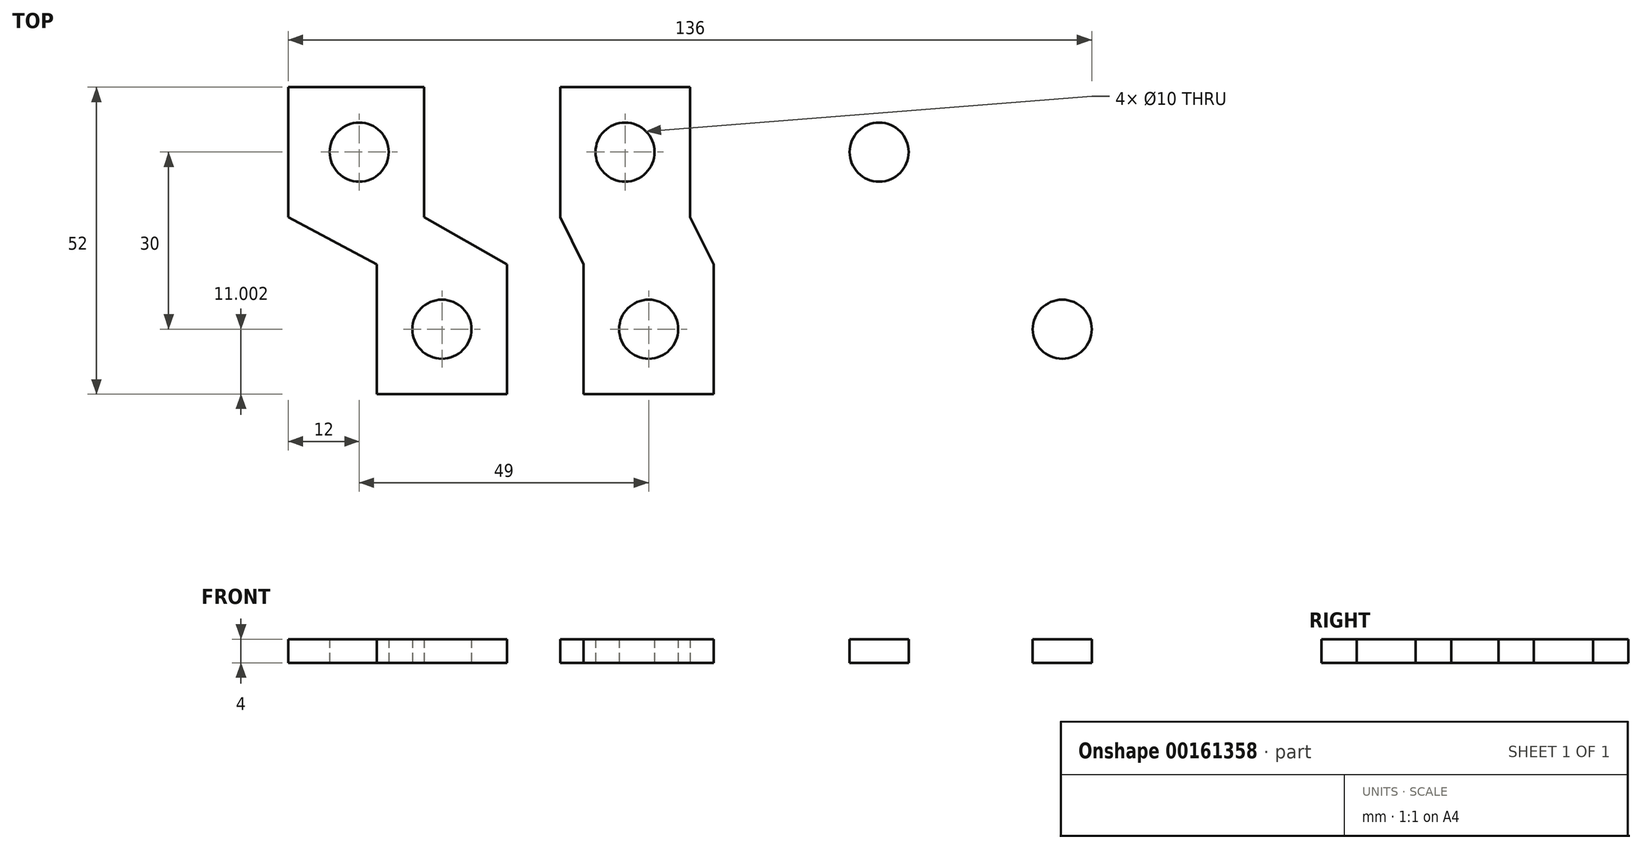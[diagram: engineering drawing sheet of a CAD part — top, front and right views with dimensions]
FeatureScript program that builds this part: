
annotation { "Feature Type Name" : "Feature", "Feature Type Description" : "" }
export const myFeature = defineFeature(function(context is Context, id is Id, definition is map)
    precondition{}
    {
        {
            var Q0;
            Q0=qCreatedBy(makeId("Top.planeOp"),FACE);
            var sketch = newSketch(context, id + "F0", { "sketchPlane" : qUnion([Q0])});
            skLineSegment(sketch, "E0.bottom", {"start": v(-56.44, 67.2) * mm, "end": v(-33.44, 67.2) * mm});
            skLineSegment(sketch, "E0.left", {"start": v(-56.44, 67.2) * mm, "end": v(-56.44, 45.2) * mm});
            skLineSegment(sketch, "E0.right", {"start": v(-33.44, 67.2) * mm, "end": v(-33.44, 45.2) * mm});
            skLineSegment(sketch, "E1.bottom", {"start": v(-41.44, 15.2) * mm, "end": v(-19.44, 15.2) * mm});
            skLineSegment(sketch, "E1.left", {"start": v(-41.44, 15.2) * mm, "end": v(-41.44, 37.2) * mm});
            skLineSegment(sketch, "E1.right", {"start": v(-19.44, 15.2) * mm, "end": v(-19.44, 37.2) * mm});
            skLineSegment(sketch, "E2", {"start": v(-56.44, 45.2) * mm, "end": v(-41.44, 37.2) * mm});
            skLineSegment(sketch, "E3", {"start": v(-33.44, 45.2) * mm, "end": v(-19.44, 37.2) * mm});
            skLineSegment(sketch, "E4.bottom", {"start": v(-10.44, 67.2) * mm, "end": v(11.56, 67.2) * mm});
            skLineSegment(sketch, "E4.left", {"start": v(-10.44, 67.2) * mm, "end": v(-10.44, 45.2) * mm});
            skLineSegment(sketch, "E4.right", {"start": v(11.56, 67.2) * mm, "end": v(11.56, 45.2) * mm});
            skLineSegment(sketch, "E5.bottom", {"start": v(-6.44, 15.2) * mm, "end": v(15.56, 15.2) * mm});
            skLineSegment(sketch, "E5.left", {"start": v(-6.44, 15.2) * mm, "end": v(-6.44, 37.2) * mm});
            skLineSegment(sketch, "E5.right", {"start": v(15.56, 15.2) * mm, "end": v(15.56, 37.2) * mm});
            skLineSegment(sketch, "E6", {"start": v(-10.44, 45.2) * mm, "end": v(-6.44, 37.2) * mm});
            skLineSegment(sketch, "E7", {"start": v(11.56, 45.2) * mm, "end": v(15.56, 37.2) * mm});
            skPoint(sketch, "E8", {"position": v(-30.44, 15.2) * mm});
            skPoint(sketch, "E9", {"position": v(-30.44, 26.2) * mm});
            skPoint(sketch, "E10", {"position": v(0.56, 56.2) * mm});
            skPoint(sketch, "E10.positionSnap0", {"position": v(0.56, 67.2) * mm});
            skPoint(sketch, "E11", {"position": v(4.56, 26.2) * mm});
            skPoint(sketch, "E11.positionSnap0", {"position": v(4.56, 15.2) * mm});
            skCircle(sketch, "E12", {"center": v(4.56, 26.2) * mm, "radius": 5 * mm});
            skCircle(sketch, "E13", {"center": v(0.56, 56.2) * mm, "radius": 5 * mm});
            skCircle(sketch, "E14", {"center": v(-30.44, 26.2) * mm, "radius": 5 * mm});
            skPoint(sketch, "E15", {"position": v(-44.44, 56.2) * mm});
            skCircle(sketch, "E16", {"center": v(-44.44, 56.2) * mm, "radius": 5 * mm});
            skLineSegment(sketch, "E17", {"start": v(15.56, 25.14) * mm, "end": v(22.06, 25.14) * mm});
            skLineSegment(sketch, "E18", {"start": v(22.06, 25.14) * mm, "end": v(22.06, 60.52) * mm});
            skPoint(sketch, "E19.MirrorP", {"position": v(43.56, 56.2) * mm});
            skCircle(sketch, "E20.MirrorC", {"center": v(43.56, 56.2) * mm, "radius": 5 * mm});
            skPoint(sketch, "E21.MirrorP", {"position": v(39.56, 26.2) * mm});
            skPoint(sketch, "E22.MirrorP", {"position": v(39.56, 15.2) * mm});
            skCircle(sketch, "E23.MirrorC", {"center": v(74.56, 26.2) * mm, "radius": 5 * mm});
            skLineSegment(sketch, "E24.MirrorCS", {"start": v(50.56, 15.2) * mm, "end": v(50.56, 37.2) * mm});
            skLineSegment(sketch, "E25.MirrorCS", {"start": v(50.56, 15.2) * mm, "end": v(28.56, 15.2) * mm});
            skLineSegment(sketch, "E26.MirrorCS", {"start": v(32.56, 67.2) * mm, "end": v(32.56, 45.2) * mm});
            skLineSegment(sketch, "E27.MirrorCS", {"start": v(54.56, 67.2) * mm, "end": v(54.56, 45.2) * mm});
            skLineSegment(sketch, "E28.MirrorCS", {"start": v(54.56, 67.2) * mm, "end": v(32.56, 67.2) * mm});
            skLineSegment(sketch, "E29.MirrorCS", {"start": v(77.56, 45.2) * mm, "end": v(63.56, 37.2) * mm});
            skLineSegment(sketch, "E30.MirrorCS", {"start": v(100.56, 45.2) * mm, "end": v(85.56, 37.2) * mm});
            skLineSegment(sketch, "E31.MirrorCS", {"start": v(63.56, 15.2) * mm, "end": v(63.56, 37.2) * mm});
            skLineSegment(sketch, "E32.MirrorCS", {"start": v(85.56, 15.2) * mm, "end": v(85.56, 37.2) * mm});
            skLineSegment(sketch, "E33.MirrorCS", {"start": v(77.56, 67.2) * mm, "end": v(77.56, 45.2) * mm});
            skPoint(sketch, "E34.MirrorP", {"position": v(74.56, 15.2) * mm});
            skLineSegment(sketch, "E35.MirrorCS", {"start": v(100.56, 67.2) * mm, "end": v(77.56, 67.2) * mm});
            skLineSegment(sketch, "E36.MirrorCS", {"start": v(32.56, 45.2) * mm, "end": v(28.56, 37.2) * mm});
            skCircle(sketch, "E37.MirrorC", {"center": v(39.56, 26.2) * mm, "radius": 5 * mm});
            skLineSegment(sketch, "E38.MirrorCS", {"start": v(85.56, 15.2) * mm, "end": v(63.56, 15.2) * mm});
            skLineSegment(sketch, "E39.MirrorCS", {"start": v(54.56, 45.2) * mm, "end": v(50.56, 37.2) * mm});
            skPoint(sketch, "E40.MirrorP", {"position": v(43.56, 67.2) * mm});
            skLineSegment(sketch, "E41.MirrorCS", {"start": v(28.56, 15.2) * mm, "end": v(28.56, 37.2) * mm});
            skCircle(sketch, "E42.MirrorC", {"center": v(88.56, 56.2) * mm, "radius": 5 * mm});
            skLineSegment(sketch, "E43.MirrorCS", {"start": v(100.56, 67.2) * mm, "end": v(100.56, 45.2) * mm});
            skSolve(sketch);
        }
        {
            var Q0;
            Q0=makeQuery(id+"F0.imprint","IMPRINT",FACE,{"disambiguationData":[TD([[makeQuery(id+"F0.imprint","IMPRINT",EDGE,{"derivedFrom":sQuery(id+"F0.wireOp",EDGE,"E0.bottom")}),-1.0]])]});
            var Q1;
            Q1=makeQuery(id+"F0.imprint","IMPRINT",FACE,{"disambiguationData":[TD([[makeQuery(id+"F0.imprint","IMPRINT",EDGE,{"derivedFrom":sQuery(id+"F0.wireOp",EDGE,"E4.bottom")}),-1.0]])]});
            var Q2;
            Q2=makeQuery(id+"F0.imprint","IMPRINT",FACE,{"disambiguationData":[TD([[makeQuery(id+"F0.imprint","IMPRINT",EDGE,{"derivedFrom":sQuery(id+"F0.wireOp",EDGE,"78a8a154-e840-4302-b636-e89f2bfbcf231.MirrorCS")}),1.0]])]});
            var Q3;
            Q3=makeQuery(id+"F0.imprint","IMPRINT",FACE,{"disambiguationData":[TD([[makeQuery(id+"F0.imprint","IMPRINT",EDGE,{"derivedFrom":sQuery(id+"F0.wireOp",EDGE,"78a8a154-e840-4302-b636-e89f2bfbcf230.MirrorCS")}),1.0]])]});
            var Q4;
            Q4=makeQuery(id+"F0.imprint","IMPRINT",FACE,{"disambiguationData":[TD([[makeQuery(id+"F0.imprint","IMPRINT",EDGE,{"derivedFrom":sQuery(id+"F0.wireOp",EDGE,"E20.MirrorC")}),1.0]])]});
            var Q5;
            Q5=makeQuery(id+"F0.imprint","IMPRINT",FACE,{"disambiguationData":[TD([[makeQuery(id+"F0.imprint","IMPRINT",EDGE,{"derivedFrom":sQuery(id+"F0.wireOp",EDGE,"E23.MirrorC")}),1.0]])]});
            extrude(context, id + "F1", {"entities" : qUnion([Q0, Q1, Q2, Q3, Q4, Q5]), "depth" : 4 * mm});
        }
    });
